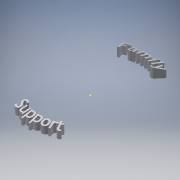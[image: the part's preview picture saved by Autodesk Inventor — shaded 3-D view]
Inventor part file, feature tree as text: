
AUTODESK INVENTOR PART (.ipt)
format: ipt  version: 2016 (Build 200138000, 138)  size: 788,480 bytes
history: native  units: in
note: dims shown in document units (in); Inventor stores cm internally (conversion verified against a paired STEP export)
features: projected_geometry x15, sketch x3, extrude x2, revolve x1
ambient origin geometry x8: Origin, YZ Plane, XZ Plane, XY Plane, X Axis, Y Axis, Z Axis, Center Point
bodies: Solid1 (feature_tree)
feature tree (21):
  revolve  "Revolution1"  [1 undecoded]
  extrude  "Extrusion1"  Depth=0.1in
  extrude  "Extrusion2"  Depth=0.275in
  sketch  "Sketch1"  dims[d0=0.8265in d1=0.175in]
  sketch  "Sketch2"  dims[d2=0.05in d3=0.1in]
  projected_geometry  "Projected Loop1"
  projected_geometry  "Projected Loop2"
  sketch  "Sketch3"  dims[d4=0.15in d5=0.275in d6=90.0deg d7=1.0in d8=0.0in d9=0.0197in d10=0.0in]
  projected_geometry  "Projected Loop3"
  projected_geometry  "Projected Loop4"
  projected_geometry  "Projected Loop5"
  projected_geometry  "Projected Loop6"
  projected_geometry  "Projected Loop7"
  projected_geometry  "Projected Loop8"
  projected_geometry  "Projected Loop9"
  projected_geometry  "Projected Loop10"
  projected_geometry  "Projected Loop11"
  projected_geometry  "Projected Loop12"
  projected_geometry  "Projected Loop13"
  projected_geometry  "Projected Loop14"
  projected_geometry  "Projected Loop15"
note: 1 required parameter value undecoded (feature->parameter linkage not recoverable at this tier; creation-order binding heuristic only, values carry confidence <= 0.55)
